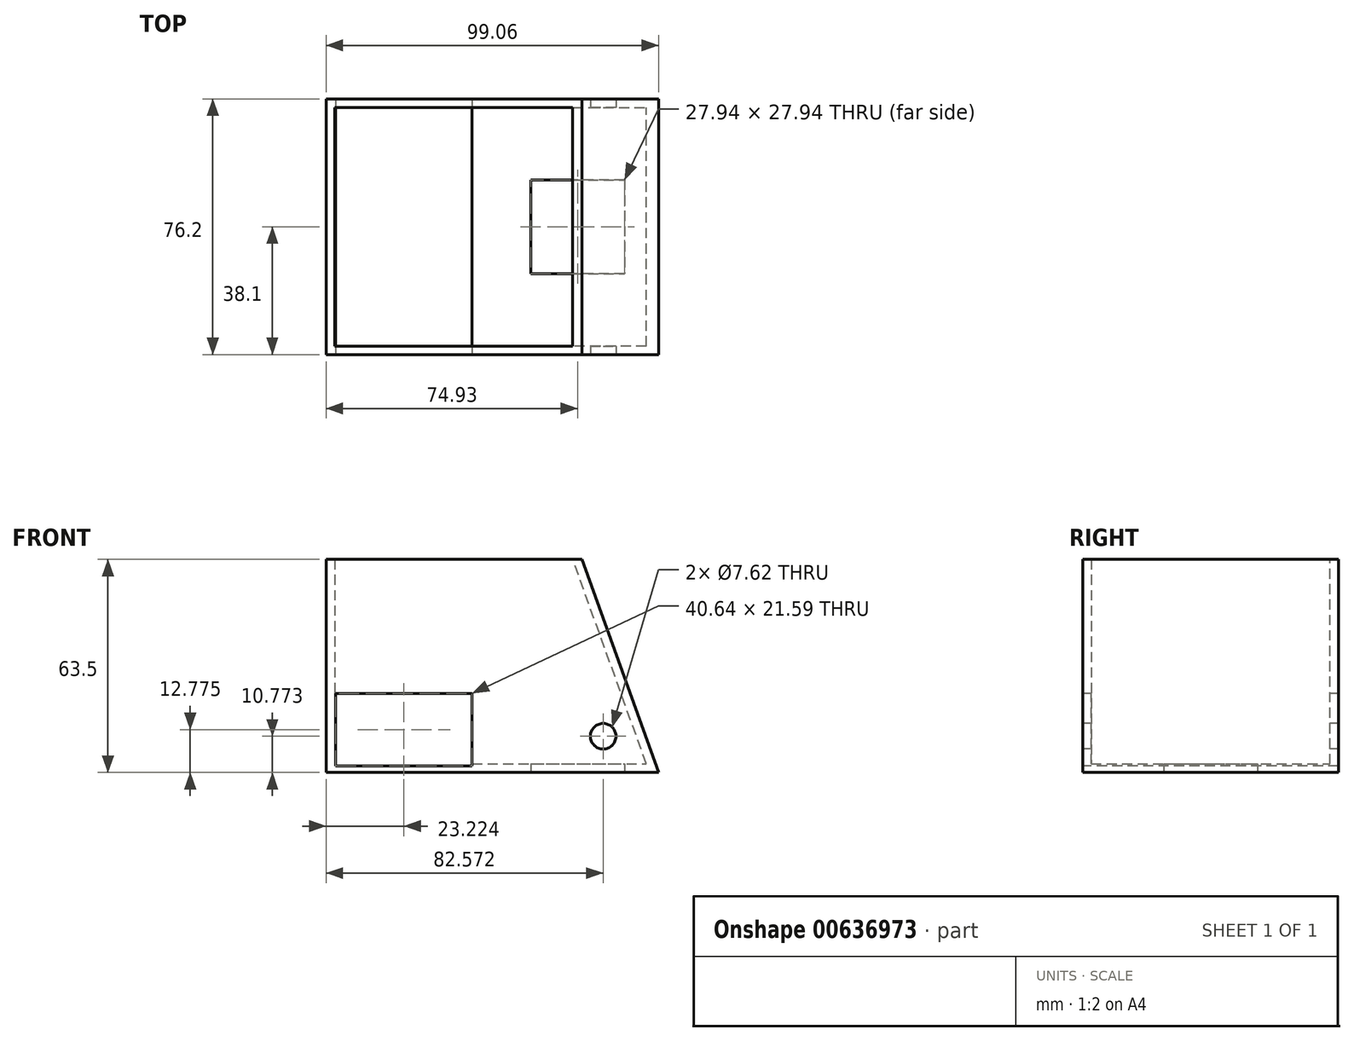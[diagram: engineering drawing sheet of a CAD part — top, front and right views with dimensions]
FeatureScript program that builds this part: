
annotation { "Feature Type Name" : "Feature", "Feature Type Description" : "" }
export const myFeature = defineFeature(function(context is Context, id is Id, definition is map)
    precondition{}
    {
        {
            var Q0;
            Q0=qCreatedBy(makeId("Front.planeOp"),FACE);
            var sketch = newSketch(context, id + "F0", { "sketchPlane" : qUnion([Q0])});
            skLineSegment(sketch, "E0.bottom", {"start": v(-60.14, 61.52) * mm, "end": v(16.06, 61.52) * mm});
            skLineSegment(sketch, "E0.top", {"start": v(-60.14, -1.98) * mm, "end": v(16.06, -1.98) * mm});
            skLineSegment(sketch, "E0.left", {"start": v(-60.14, 61.52) * mm, "end": v(-60.14, -1.98) * mm});
            skLineSegment(sketch, "E0.right", {"start": v(16.06, 61.52) * mm, "end": v(16.06, -1.98) * mm});
            skLineSegment(sketch, "E1", {"start": v(16.06, -1.98) * mm, "end": v(38.92, -1.98) * mm});
            skLineSegment(sketch, "E2", {"start": v(38.92, -1.98) * mm, "end": v(16.06, 61.52) * mm});
            skSolve(sketch);
        }
        {
            var Q0;
            Q0=makeQuery(id+"F0.imprint","IMPRINT",FACE,{"disambiguationData":[TD([[makeQuery(id+"F0.imprint","IMPRINT",EDGE,{"derivedFrom":sQuery(id+"F0.wireOp",EDGE,"E0.bottom")}),-1.0]])]});
            var Q1;
            Q1=makeQuery(id+"F0.imprint","IMPRINT",FACE,{"disambiguationData":[TD([[makeQuery(id+"F0.imprint","IMPRINT",EDGE,{"derivedFrom":sQuery(id+"F0.wireOp",EDGE,"E0.right")}),1.0]])]});
            extrude(context, id + "F1", {"entities" : qUnion([Q0, Q1]), "depth" : 76.2 * mm, "offsetDistance" : 25.4 * mm});
        }
        {
            var Q0;
            Q0=makeQuery(id+"F1.opExtrude","SWEPT_FACE",FACE,{"disambiguationData":[OSD([sQuery(id+"F0.wireOp",EDGE,"E0.bottom")])]});
            shell(context, id + "F2", {"entities" : qUnion([Q0]), "thickness" : 2.54 * mm});
        }
        {
            var Q0;
            Q0=makeQuery(id+"F1.opExtrude","SWEPT_FACE",FACE,{"disambiguationData":[OSD([sQuery(id+"F0.wireOp",EDGE,"E0.top"),sQuery(id+"F0.wireOp",EDGE,"E1")])]});
            var sketch = newSketch(context, id + "F3", { "sketchPlane" : qUnion([Q0])});
            skLineSegment(sketch, "E3", {"start": v(28.76, 0) * mm, "end": v(28.76, 24.13) * mm});
            skLineSegment(sketch, "E4.bottom", {"start": v(28.76, 24.13) * mm, "end": v(0.82, 24.13) * mm});
            skLineSegment(sketch, "E4.top", {"start": v(28.76, 52.07) * mm, "end": v(0.82, 52.07) * mm});
            skLineSegment(sketch, "E4.left", {"start": v(28.76, 24.13) * mm, "end": v(28.76, 52.07) * mm});
            skLineSegment(sketch, "E4.right", {"start": v(0.82, 24.13) * mm, "end": v(0.82, 52.07) * mm});
            skLineSegment(sketch, "E5", {"start": v(0.82, 24.13) * mm, "end": v(-60.14, 24.13) * mm});
            skSolve(sketch);
        }
        {
            var Q0;
            Q0=makeQuery(id+"F3.imprint","IMPRINT",FACE,{"disambiguationData":[TD([[makeQuery(id+"F3.imprint","IMPRINT",EDGE,{"derivedFrom":sQuery(id+"F3.wireOp",EDGE,"E4.bottom")}),-1.0]])]});
            extrude(context, id + "F4", {"entities" : qUnion([Q0]), "operationType" : NewBodyOperationType.REMOVE, "oppositeDirection" : true, "depth" : 16.26 * mm, "offsetDistance" : 25.4 * mm});
        }
        {
            var Q0;
            Q0=makeQuery(id+"F1.opExtrude","CAP_FACE",FACE,{"disambiguationData":[OSD([sQuery(id+"F0.wireOp",EDGE,"E0.bottom"),sQuery(id+"F0.wireOp",EDGE,"E0.top"),sQuery(id+"F0.wireOp",EDGE,"E0.left"),sQuery(id+"F0.wireOp",EDGE,"E1"),sQuery(id+"F0.wireOp",EDGE,"E2")])],"isStart":false});
            var sketch = newSketch(context, id + "F5", { "sketchPlane" : qUnion([Q0])});
            skLineSegment(sketch, "E6", {"start": v(-57.24, -1.98) * mm, "end": v(-57.24, 0) * mm});
            skLineSegment(sketch, "E7.bottom", {"start": v(-57.24, 0) * mm, "end": v(-16.6, 0) * mm});
            skLineSegment(sketch, "E7.top", {"start": v(-57.24, 21.6) * mm, "end": v(-16.6, 21.6) * mm});
            skLineSegment(sketch, "E7.left", {"start": v(-57.24, 0) * mm, "end": v(-57.24, 21.6) * mm});
            skLineSegment(sketch, "E7.right", {"start": v(-16.6, 0) * mm, "end": v(-16.6, 21.6) * mm});
            skSolve(sketch);
        }
        {
            var Q0;
            Q0 = qSketchRegion(id + "F5", true);
            extrude(context, id + "F6", {"entities" : qUnion([Q0]), "operationType" : NewBodyOperationType.REMOVE, "oppositeDirection" : true, "depth" : 100.08 * mm, "offsetDistance" : 25.4 * mm});
        }
        {
            var Q0;
            Q0=makeQuery(id+"F1.opExtrude","CAP_FACE",FACE,{"disambiguationData":[OSD([sQuery(id+"F0.wireOp",EDGE,"E0.bottom"),sQuery(id+"F0.wireOp",EDGE,"E0.top"),sQuery(id+"F0.wireOp",EDGE,"E0.left"),sQuery(id+"F0.wireOp",EDGE,"E1"),sQuery(id+"F0.wireOp",EDGE,"E2")])],"isStart":false});
            var sketch = newSketch(context, id + "F7", { "sketchPlane" : qUnion([Q0])});
            skCircle(sketch, "E8", {"center": v(22.43, 8.8) * mm, "radius": 3.81 * mm});
            skSolve(sketch);
        }
        {
            var Q0;
            Q0=makeQuery(id+"F7.imprint","IMPRINT",FACE,{"disambiguationData":[TD([[makeQuery(id+"F7.imprint","IMPRINT",EDGE,{"derivedFrom":sQuery(id+"F7.wireOp",EDGE,"E8")}),1.0]])]});
            extrude(context, id + "F8", {"entities" : qUnion([Q0]), "operationType" : NewBodyOperationType.REMOVE, "oppositeDirection" : true, "depth" : 99.82 * mm, "offsetDistance" : 25.4 * mm});
        }
    });
